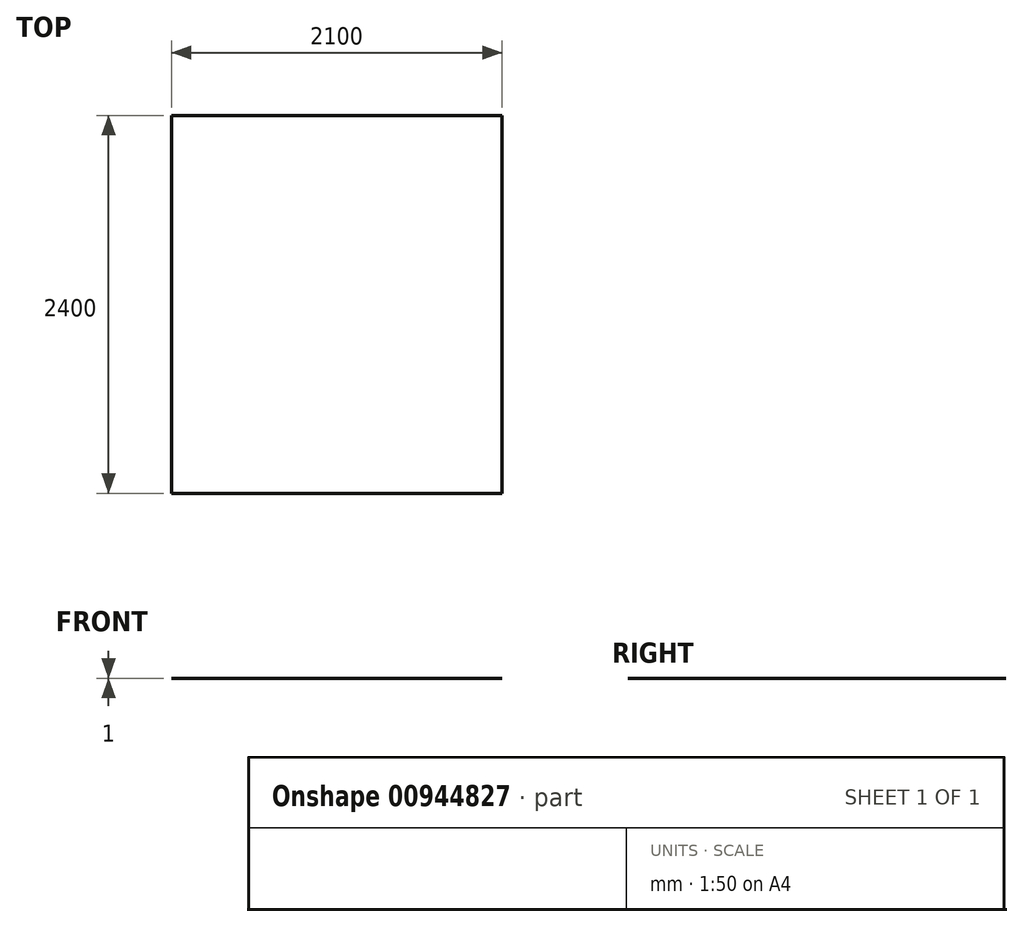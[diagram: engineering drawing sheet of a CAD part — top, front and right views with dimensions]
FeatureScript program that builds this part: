
annotation { "Feature Type Name" : "Feature", "Feature Type Description" : "" }
export const myFeature = defineFeature(function(context is Context, id is Id, definition is map)
    precondition{}
    {
        {
            var Q0;
            Q0=qCreatedBy(makeId("Top.planeOp"),FACE);
            var sketch = newSketch(context, id + "F0", { "sketchPlane" : qUnion([Q0])});
            skLineSegment(sketch, "E0.bottom", {"start": v(550, -400) * mm, "end": v(-550, -400) * mm});
            skLineSegment(sketch, "E0.top", {"start": v(550, 400) * mm, "end": v(-550, 400) * mm});
            skLineSegment(sketch, "E0.left", {"start": v(550, -400) * mm, "end": v(550, 400) * mm});
            skLineSegment(sketch, "E0.right", {"start": v(-550, -400) * mm, "end": v(-550, 400) * mm});
            skPoint(sketch, "E0.middle", {"position": v(0, 0) * mm});
            skLineSegment(sketch, "E1.bottom", {"start": v(-750, -1200) * mm, "end": v(1350, -1200) * mm});
            skLineSegment(sketch, "E1.top", {"start": v(-750, 1200) * mm, "end": v(1350, 1200) * mm});
            skLineSegment(sketch, "E1.left", {"start": v(-750, -1200) * mm, "end": v(-750, 1200) * mm});
            skLineSegment(sketch, "E1.right", {"start": v(1350, -1200) * mm, "end": v(1350, 1200) * mm});
            skLineSegment(sketch, "E2", {"start": v(-750, 1200) * mm, "end": v(-750, 1500) * mm});
            skLineSegment(sketch, "E3", {"start": v(-750, -1200) * mm, "end": v(-750, -1500) * mm});
            skLineSegment(sketch, "E4", {"start": v(-750, 1350) * mm, "end": v(-893.4, 1500) * mm});
            skLineSegment(sketch, "E5", {"start": v(-750, 1200) * mm, "end": v(-893.4, 1350) * mm});
            skLineSegment(sketch, "E6", {"start": v(-750, 1057.45) * mm, "end": v(-893.4, 1207.45) * mm});
            skLineSegment(sketch, "E7", {"start": v(-750, 907.45) * mm, "end": v(-893.4, 1057.45) * mm});
            skLineSegment(sketch, "E8", {"start": v(-750, 759.55) * mm, "end": v(-893.4, 909.55) * mm});
            skLineSegment(sketch, "E9", {"start": v(-750, 609.55) * mm, "end": v(-893.4, 759.55) * mm});
            skLineSegment(sketch, "E10", {"start": v(-750, 467) * mm, "end": v(-893.4, 617) * mm});
            skLineSegment(sketch, "E11", {"start": v(-750, 317) * mm, "end": v(-893.4, 467) * mm});
            skLineSegment(sketch, "E12", {"start": v(-744.35, 182.48) * mm, "end": v(-887.74, 332.48) * mm});
            skLineSegment(sketch, "E13", {"start": v(-744.35, 32.48) * mm, "end": v(-887.74, 182.48) * mm});
            skLineSegment(sketch, "E14", {"start": v(-744.35, -110.07) * mm, "end": v(-887.74, 39.93) * mm});
            skLineSegment(sketch, "E15", {"start": v(-744.35, -260.07) * mm, "end": v(-887.74, -110.07) * mm});
            skLineSegment(sketch, "E16", {"start": v(-744.35, -407.96) * mm, "end": v(-887.74, -257.96) * mm});
            skLineSegment(sketch, "E17", {"start": v(-744.35, -557.96) * mm, "end": v(-887.74, -407.96) * mm});
            skLineSegment(sketch, "E18", {"start": v(-744.35, -700.52) * mm, "end": v(-887.74, -550.52) * mm});
            skLineSegment(sketch, "E19", {"start": v(-744.35, -850.52) * mm, "end": v(-887.74, -700.52) * mm});
            skLineSegment(sketch, "E20", {"start": v(-750, -992.22) * mm, "end": v(-893.4, -842.22) * mm});
            skLineSegment(sketch, "E21", {"start": v(-750, -1134.77) * mm, "end": v(-893.4, -984.77) * mm});
            skLineSegment(sketch, "E22", {"start": v(-750, -1284.77) * mm, "end": v(-893.4, -1134.77) * mm});
            skLineSegment(sketch, "E23", {"start": v(-750, -1431.66) * mm, "end": v(-893.4, -1281.66) * mm});
            skSolve(sketch);
        }
        {
            var Q0;
            Q0=makeQuery(id+"F0.imprint","IMPRINT",FACE,{"disambiguationData":[TD([[makeQuery(id+"F0.imprint","IMPRINT",EDGE,{"derivedFrom":sQuery(id+"F0.wireOp",EDGE,"E0.bottom")}),-1.0]])]});
            var Q1;
            Q1=makeQuery(id+"F0.imprint","IMPRINT",FACE,{"disambiguationData":[TD([[makeQuery(id+"F0.imprint","IMPRINT",EDGE,{"derivedFrom":sQuery(id+"F0.wireOp",EDGE,"E0.bottom")}),1.0]])]});
            extrude(context, id + "F1", {"entities" : qUnion([Q0, Q1]), "depth" : 1 * mm, "offsetDistance" : 25 * mm});
        }
    });
